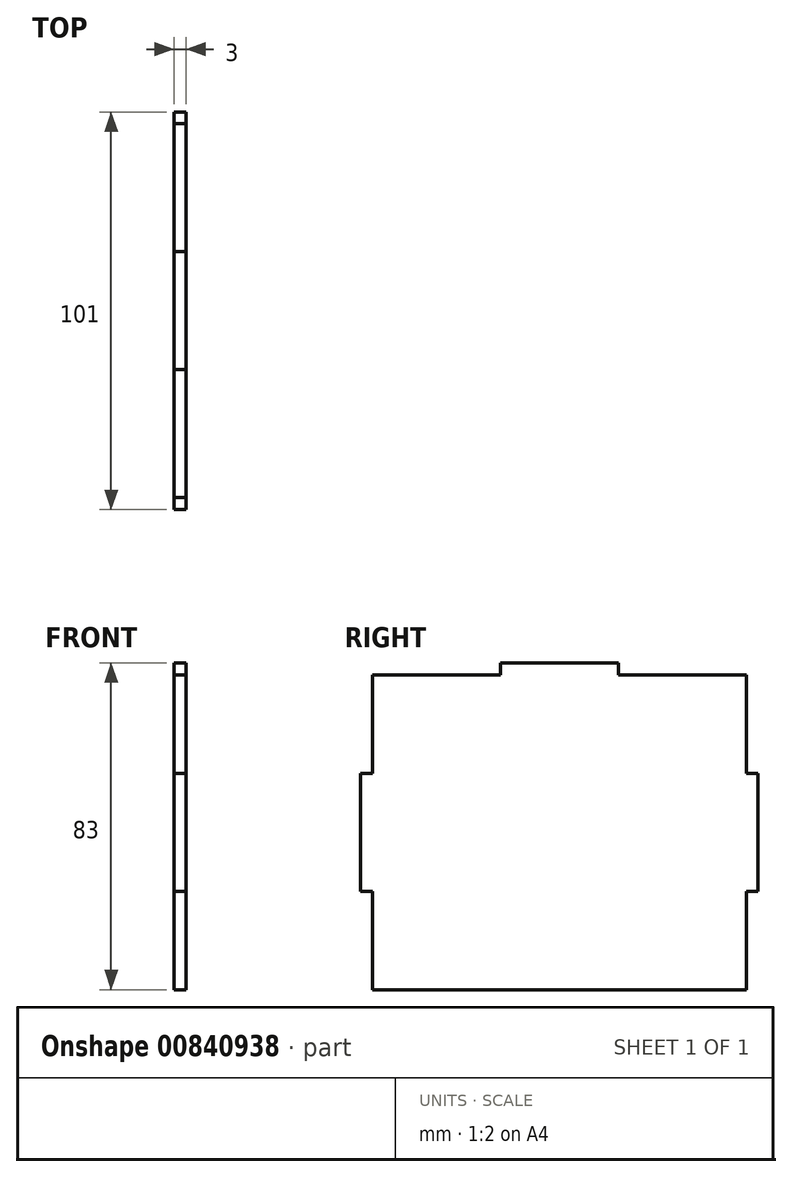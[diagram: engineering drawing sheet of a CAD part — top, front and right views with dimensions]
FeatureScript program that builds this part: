
annotation { "Feature Type Name" : "Feature", "Feature Type Description" : "" }
export const myFeature = defineFeature(function(context is Context, id is Id, definition is map)
    precondition{}
    {
        {
            var Q0;
            Q0=qCreatedBy(makeId("Right.planeOp"),FACE);
            var sketch = newSketch(context, id + "F0", { "sketchPlane" : qUnion([Q0])});
            skLineSegment(sketch, "E0.bottom", {"start": v(-38.72, 42.35) * mm, "end": v(56.28, 42.35) * mm});
            skLineSegment(sketch, "E0.top", {"start": v(-38.72, -37.65) * mm, "end": v(56.28, -37.65) * mm});
            skLineSegment(sketch, "E0.left", {"start": v(-38.72, 42.35) * mm, "end": v(-38.72, -37.65) * mm});
            skLineSegment(sketch, "E0.right", {"start": v(56.28, 42.35) * mm, "end": v(56.28, -37.65) * mm});
            skLineSegment(sketch, "E1.bottom", {"start": v(-38.72, 17.35) * mm, "end": v(-41.72, 17.35) * mm});
            skLineSegment(sketch, "E1.top", {"start": v(-38.72, -12.65) * mm, "end": v(-41.72, -12.65) * mm});
            skLineSegment(sketch, "E1.left", {"start": v(-38.72, 17.35) * mm, "end": v(-38.72, -12.65) * mm});
            skLineSegment(sketch, "E1.right", {"start": v(-41.72, 17.35) * mm, "end": v(-41.72, -12.65) * mm});
            skLineSegment(sketch, "E2", {"start": v(8.78, 42.35) * mm, "end": v(8.78, 21.5) * mm, "construction": true});
            skLineSegment(sketch, "E3.MirrorCS", {"start": v(56.28, 17.35) * mm, "end": v(59.28, 17.35) * mm});
            skLineSegment(sketch, "E4.MirrorCS", {"start": v(56.28, -12.65) * mm, "end": v(59.28, -12.65) * mm});
            skLineSegment(sketch, "E5.MirrorCS", {"start": v(56.28, 17.35) * mm, "end": v(56.28, -12.65) * mm});
            skLineSegment(sketch, "E6.MirrorCS", {"start": v(59.28, 17.35) * mm, "end": v(59.28, -12.65) * mm});
            skLineSegment(sketch, "E7.bottom", {"start": v(-6.22, 45.35) * mm, "end": v(23.78, 45.35) * mm});
            skLineSegment(sketch, "E7.top", {"start": v(-6.22, 42.35) * mm, "end": v(23.78, 42.35) * mm});
            skLineSegment(sketch, "E7.left", {"start": v(-6.22, 45.35) * mm, "end": v(-6.22, 42.35) * mm});
            skLineSegment(sketch, "E7.right", {"start": v(23.78, 45.35) * mm, "end": v(23.78, 42.35) * mm});
            skSolve(sketch);
        }
        {
            var Q0;
            Q0 = qSketchRegion(id + "F0", true);
            extrude(context, id + "F1", {"entities" : qUnion([Q0]), "depth" : 3 * mm, "offsetDistance" : 25 * mm});
        }
    });
